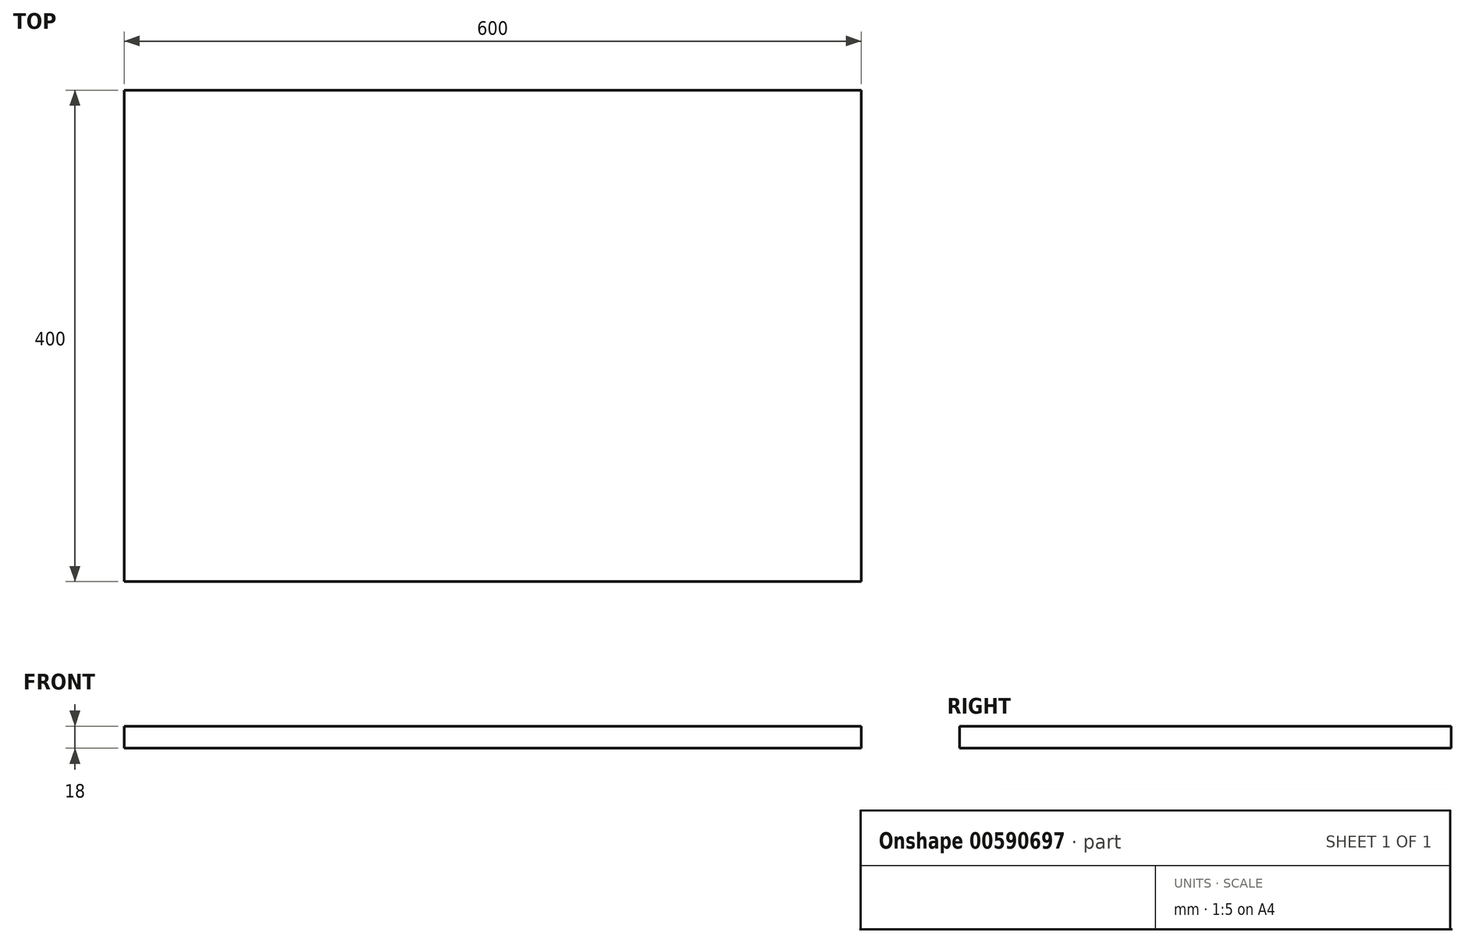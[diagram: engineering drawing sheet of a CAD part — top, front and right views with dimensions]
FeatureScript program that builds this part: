
annotation { "Feature Type Name" : "Feature", "Feature Type Description" : "" }
export const myFeature = defineFeature(function(context is Context, id is Id, definition is map)
    precondition{}
    {
        {
            assignVariable(context, id + "F0", {"name" : "longueur", "anyValue" : 400});
        }
        {
            var Q0;
            Q0=qCreatedBy(makeId("Front.planeOp"),FACE);
            var sketch = newSketch(context, id + "F1", { "sketchPlane" : qUnion([Q0])});
            skLineSegment(sketch, "E0.bottom", {"start": v(-300, 9) * mm, "end": v(300, 9) * mm});
            skLineSegment(sketch, "E0.top", {"start": v(-300, -9) * mm, "end": v(300, -9) * mm});
            skLineSegment(sketch, "E0.left", {"start": v(-300, 9) * mm, "end": v(-300, -9) * mm});
            skLineSegment(sketch, "E0.right", {"start": v(300, 9) * mm, "end": v(300, -9) * mm});
            skPoint(sketch, "E0.middle", {"position": v(0, 0) * mm});
            skSolve(sketch);
        }
        {
            var Q0;
            Q0=qSketchRegion(id+"F1",true);
            extrude(context, id + "F2", {"entities" : qUnion([Q0]), "endBound" : BoundingType.SYMMETRIC, "depth" : (getVariable(context, 'longueur')) * mm, "offsetDistance" : 25 * mm});
        }
    });
